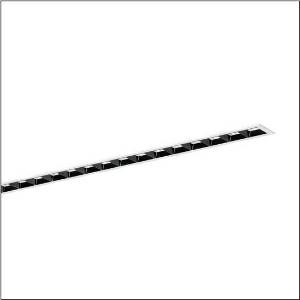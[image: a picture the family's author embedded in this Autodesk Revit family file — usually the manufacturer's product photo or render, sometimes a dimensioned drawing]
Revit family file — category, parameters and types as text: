
# Revit family: silica_21_51mx12tbt5w
name_source: partatom
category: Lighting Fixtures
units: mm (PartAtom-declared; Revit-internal decimal feet)

## family parameters
Cut with Voids When Loaded = No
Host = Face
Light Source = No
Part Type = Normal
Room Calculation Point = No
Round Connector Dimension = Use Diameter
Shared = No

## types (1)
- --- (1 x LED, 4650 lm, 40.2 W, 6500K)
    Apparent Load = 40 VA
    CIE Flux Codes = 84 100 100 100 100
    Color Rendering = 80
    Color Temperature = 6500K
    Default Elevation = 1800 mm
    Description = Silica 21, office luminaire, primary light control with darklight reflector, of PMMA, black, CAT 2 (L<= 3000cd/m²), light emission: direct distribution, primary light characteristic: symmetric, installation type: recessed, LED, rated luminous flux: 4.650lm, luminous efficacy: 110lm/W, light colour: 8tw, colour temperature: 2700..6500K, control gear: DALI DT8, with terminal, 3+2-pole, max. 2.5mm², mains connection: 220..240V, AC, 50/60Hz, rated input power: 42.2W, luminaire housing, of aluminium, traffic white (RAL 9016), length: 1.528mm, width: 79mm, height: 53mm, protection rating (complete): IP20, insulation class (complete): insulation class I (protective earthing), certification: CE, ENEC, VDE, permissible operating ambient temperature: 0..+35°C, standard: EN 50419, packaging unit: 1 piece
    Height = 0 mm  [stored 0 ft]
    Lamp = 1 x LED
    Lamp Light Flux = 4650 lm
    Lamp Power = 40.2 W
    Lamp count = 1
    Length = 1527 mm
    Luminous efficacy = 116 lm/W
    Manufacturer = Siteco
    ModVariant = No
    Model = 51MX12TBT5W
    Mounting Place = Ceiling
    Mounting Type = Recessed
    Number of Poles = 1
    OnlyDefault = Yes
    Power Factor = 1
    Product Name = Silica 21
    Product group = office luminaire | ceiling recessed
    ProductGroupID = 400
    Protection Class = Protection class I
    Protection Degree = IP 20
    RLX_Detail_Level = 1
    RLX_Emergency_Light_Flux = 0 lm
    RLX_Emergency_Type = 0
    RLX_Emergency_Type_DB = No
    RlxData = <blob elided: 39109 chars, md5=536c3a8e>
    Socket = socket
    Standby Power = 0 W
    System Light Flux = 4650 lm
    System Power = 40 W
    Type Comments = individual setting
    Type Image = l_1335880.jpg
    URL = http://relux.com
    VarID = @adj_139667
    Voltage = 0 V
    Weight = 0.00 kg
    Width = 79 mm

note: [stored X ft] marks values corroborated as IEEE doubles in the binary element streams (Revit-internal decimal feet)

## geometry (parser evidence)
native form markers: Blend x4, Sweep x10
no freeform markers — native parametric forms only
